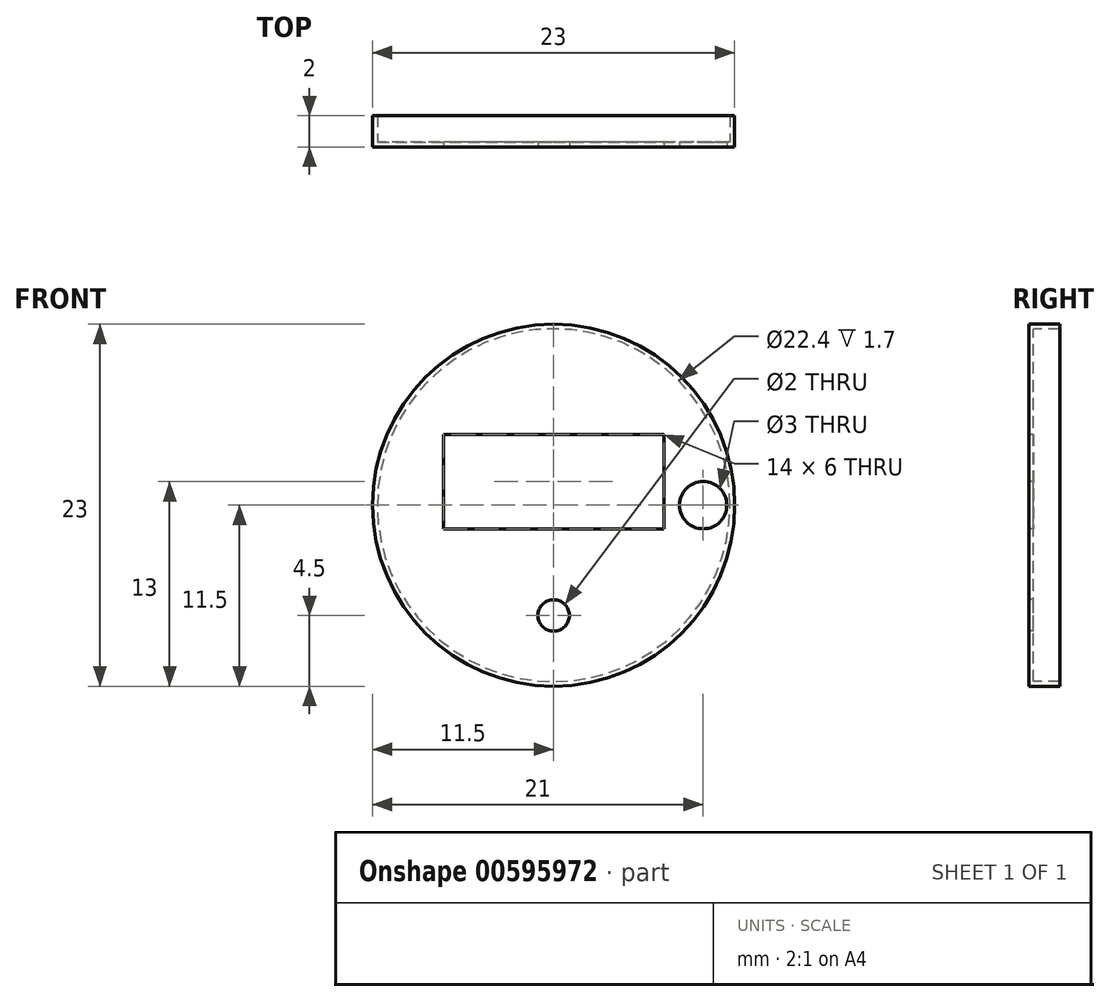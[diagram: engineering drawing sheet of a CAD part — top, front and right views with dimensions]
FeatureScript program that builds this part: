
annotation { "Feature Type Name" : "Feature", "Feature Type Description" : "" }
export const myFeature = defineFeature(function(context is Context, id is Id, definition is map)
    precondition{}
    {
        {
            var Q0;
            Q0=qCreatedBy(makeId("Front.planeOp"),FACE);
            var sketch = newSketch(context, id + "F0", { "sketchPlane" : qUnion([Q0])});
            skCircle(sketch, "E0", {"center": v(0, 0) * mm, "radius": 11.5 * mm});
            skLineSegment(sketch, "E1.bottom", {"start": v(7, 4.5) * mm, "end": v(-7, 4.5) * mm, "construction": true});
            skLineSegment(sketch, "E1.top", {"start": v(7, -1.5) * mm, "end": v(-7, -1.5) * mm, "construction": true});
            skLineSegment(sketch, "E1.left", {"start": v(7, 4.5) * mm, "end": v(7, -1.5) * mm, "construction": true});
            skLineSegment(sketch, "E1.right", {"start": v(-7, 4.5) * mm, "end": v(-7, -1.5) * mm, "construction": true});
            skLineSegment(sketch, "E2", {"start": v(0, 4.5) * mm, "end": v(0, 0) * mm, "construction": true});
            skCircle(sketch, "E3", {"center": v(0, -7) * mm, "radius": 1 * mm, "construction": true});
            skCircle(sketch, "E4", {"center": v(9.5, 0) * mm, "radius": 1.5 * mm, "construction": true});
            skSolve(sketch);
        }
        {
            var Q0;
            Q0=qCreatedBy(makeId("Front.planeOp"),FACE);
            var sketch = newSketch(context, id + "F1", { "sketchPlane" : qUnion([Q0])});
            skCircle(sketch, "E5", {"center": v(0, 0) * mm, "radius": 11.5 * mm, "construction": true});
            skLineSegment(sketch, "E6.bottom", {"start": v(7, 4.5) * mm, "end": v(-7, 4.5) * mm});
            skLineSegment(sketch, "E6.top", {"start": v(7, -1.5) * mm, "end": v(-7, -1.5) * mm});
            skLineSegment(sketch, "E6.left", {"start": v(7, 4.5) * mm, "end": v(7, -1.5) * mm});
            skLineSegment(sketch, "E6.right", {"start": v(-7, 4.5) * mm, "end": v(-7, -1.5) * mm});
            skLineSegment(sketch, "E7", {"start": v(0, 4.5) * mm, "end": v(0, 0) * mm, "construction": true});
            skCircle(sketch, "E8", {"center": v(0, -7) * mm, "radius": 1 * mm});
            skCircle(sketch, "E9", {"center": v(9.5, 0) * mm, "radius": 1.5 * mm});
            skSolve(sketch);
        }
        {
            var Q0;
            Q0 = qSketchRegion(id + "F0", true);
            extrude(context, id + "F2", {"entities" : qUnion([Q0]), "oppositeDirection" : true, "depth" : 2 * mm, "offsetDistance" : 25.4 * mm});
        }
        {
            var Q0;
            Q0=makeQuery(id+"F2.opExtrude","CAP_FACE",FACE,{"disambiguationData":[OSD([sQuery(id+"F0.wireOp",EDGE,"E0"),sQuery(id+"F0.wireOp",EDGE,"E1.bottom"),sQuery(id+"F0.wireOp",EDGE,"E1.top"),sQuery(id+"F0.wireOp",EDGE,"E1.left"),sQuery(id+"F0.wireOp",EDGE,"E1.right"),sQuery(id+"F0.wireOp",EDGE,"E3"),sQuery(id+"F0.wireOp",EDGE,"E4")])],"isStart":false});
            shell(context, id + "F3", {"entities" : qUnion([Q0]), "thickness" : 0.3 * mm});
        }
        {
            var Q0;
            Q0 = qSketchRegion(id + "F1", true);
            var Q1;
            Q1=sQuery(id+"F1.wireOp",EDGE,"E5");
            var Q2;
            Q2=sQuery(id+"F1.wireOp",EDGE,"E6.top");
            var Q3;
            Q3=sQuery(id+"F1.wireOp",EDGE,"E6.right");
            var Q4;
            Q4=sQuery(id+"F1.wireOp",EDGE,"E6.bottom");
            var Q5;
            Q5=sQuery(id+"F1.wireOp",EDGE,"E6.left");
            var Q6;
            Q6=sQuery(id+"F1.wireOp",EDGE,"E9");
            var Q7;
            Q7=sQuery(id+"F1.wireOp",EDGE,"E8");
            extrude(context, id + "F4", {"entities" : qUnion([Q0]), "operationType" : NewBodyOperationType.REMOVE, "surfaceEntities" : qUnion([Q1, Q2, Q3, Q4, Q5, Q6, Q7]), "endBound" : BoundingType.THROUGH_ALL, "oppositeDirection" : true, "depth" : 25.4 * mm, "offsetDistance" : 25.4 * mm});
        }
    });
